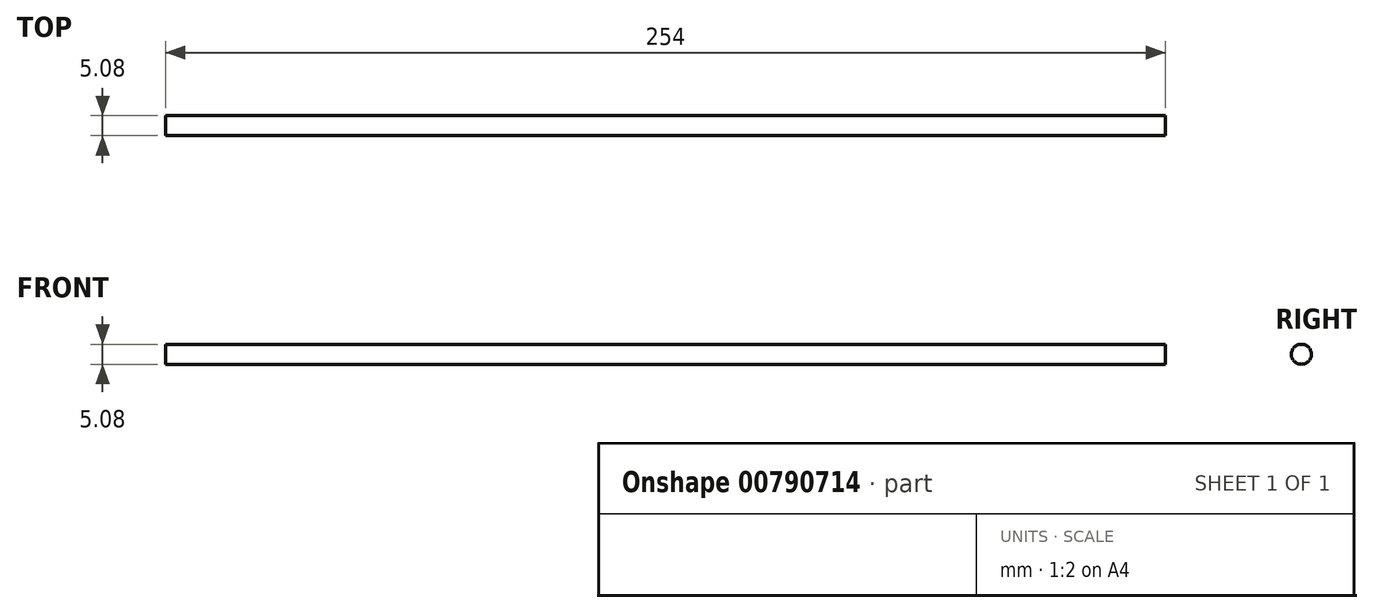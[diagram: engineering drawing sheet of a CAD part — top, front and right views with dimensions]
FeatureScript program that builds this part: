
annotation { "Feature Type Name" : "Feature", "Feature Type Description" : "" }
export const myFeature = defineFeature(function(context is Context, id is Id, definition is map)
    precondition{}
    {
        {
            var Q0;
            Q0=qCreatedBy(makeId("Right.planeOp"),FACE);
            var sketch = newSketch(context, id + "F0", { "sketchPlane" : qUnion([Q0])});
            skCircle(sketch, "E0", {"center": v(0, 0) * mm, "radius": 2.54 * mm});
            skSolve(sketch);
        }
        {
            var Q0;
            Q0 = qSketchRegion(id + "F0", true);
            extrude(context, id + "F1", {"entities" : qUnion([Q0]), "depth" : 254 * mm, "offsetDistance" : 25.4 * mm});
        }
    });
